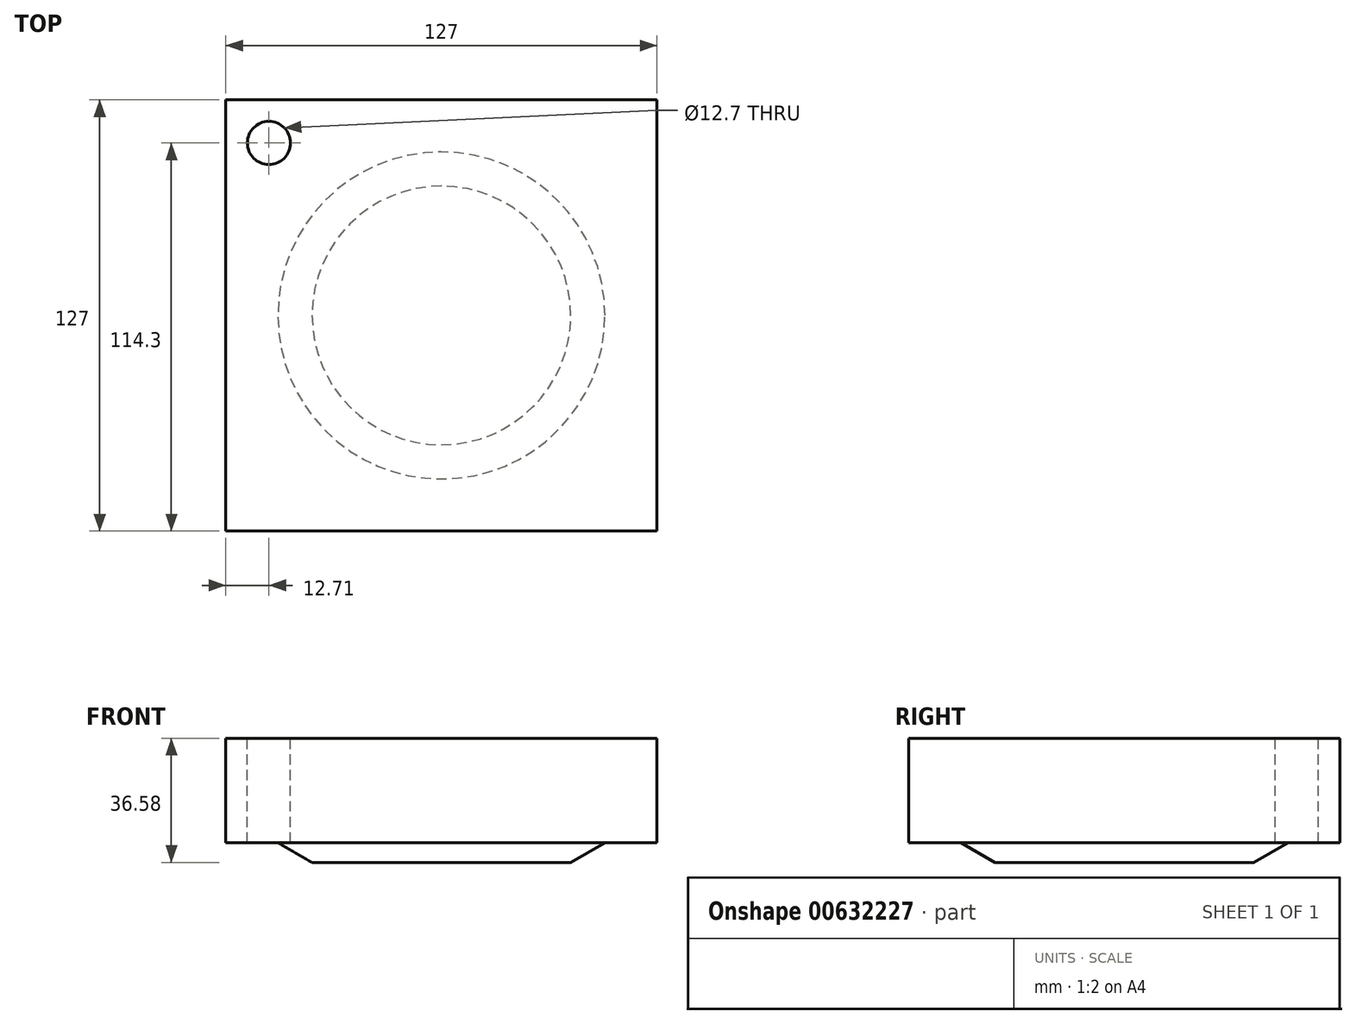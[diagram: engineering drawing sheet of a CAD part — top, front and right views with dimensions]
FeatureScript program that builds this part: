
annotation { "Feature Type Name" : "Feature", "Feature Type Description" : "" }
export const myFeature = defineFeature(function(context is Context, id is Id, definition is map)
    precondition{}
    {
        {
            var Q0;
            Q0=qCreatedBy(makeId("Front.planeOp"),FACE);
            var sketch = newSketch(context, id + "F0", { "sketchPlane" : qUnion([Q0])});
            skLineSegment(sketch, "E0", {"start": v(38.1, 1.52) * mm, "end": v(0, 1.52) * mm});
            skLineSegment(sketch, "E1", {"start": v(0, 1.52) * mm, "end": v(0, 0) * mm});
            skLineSegment(sketch, "E2", {"start": v(38.1, 1.52) * mm, "end": v(48.16, 7.33) * mm});
            skPoint(sketch, "E3.middle", {"position": v(0, 1.52) * mm});
            skLineSegment(sketch, "E4", {"start": v(0, 1.52) * mm, "end": v(38.1, 1.52) * mm});
            skLineSegment(sketch, "E5", {"start": v(48.16, 7.33) * mm, "end": v(92.57, 7.33) * mm});
            skLineSegment(sketch, "E6", {"start": v(92.57, 7.33) * mm, "end": v(92.57, 0) * mm});
            skLineSegment(sketch, "E7", {"start": v(0, 0) * mm, "end": v(92.57, 0) * mm});
            skSolve(sketch);
        }
        {
            var Q0;
            Q0=qCreatedBy(makeId("Front.planeOp"),FACE);
            var sketch = newSketch(context, id + "F1", { "sketchPlane" : qUnion([Q0])});
            skLineSegment(sketch, "E8.bottom", {"start": v(-63.5, 0) * mm, "end": v(63.5, 0) * mm});
            skLineSegment(sketch, "E8.top", {"start": v(-63.5, 38.1) * mm, "end": v(63.5, 38.1) * mm});
            skLineSegment(sketch, "E8.left", {"start": v(-63.5, 0) * mm, "end": v(-63.5, 38.1) * mm});
            skLineSegment(sketch, "E8.right", {"start": v(63.5, 0) * mm, "end": v(63.5, 38.1) * mm});
            skSolve(sketch);
        }
        {
            var Q0;
            Q0=makeQuery(id+"F1.imprint","IMPRINT",FACE,{"disambiguationData":[TD([[makeQuery(id+"F1.imprint","IMPRINT",EDGE,{"derivedFrom":sQuery(id+"F1.wireOp",EDGE,"E8.bottom")}),1.0]])]});
            extrude(context, id + "F2", {"entities" : qUnion([Q0]), "endBound" : BoundingType.SYMMETRIC, "depth" : 127 * mm, "offsetDistance" : 25.4 * mm});
        }
        {
            var Q0;
            Q0=makeQuery(id+"F0.imprint","IMPRINT",FACE,{"disambiguationData":[TD([[makeQuery(id+"F0.imprint","IMPRINT",EDGE,{"derivedFrom":sQuery(id+"F0.wireOp",EDGE,"E1")}),1.0]])]});
            var Q1;
            Q1=sQuery(id+"F0.wireOp",EDGE,"E1");
            revolve(context, id + "F3", {"operationType" : NewBodyOperationType.REMOVE, "entities" : qUnion([Q0]), "axis" : qUnion([Q1]), "revolveType" : RevolveType.FULL, "oppositeDirection" : true});
        }
        {
            var Q0;
            Q0=qCreatedBy(makeId("Top.planeOp"),FACE);
            var sketch = newSketch(context, id + "F4", { "sketchPlane" : qUnion([Q0])});
            skLineSegment(sketch, "E9", {"start": v(-50.8, 50.8) * mm, "end": v(0, 50.8) * mm});
            skLineSegment(sketch, "E10", {"start": v(-50.8, 50.8) * mm, "end": v(-50.8, 0) * mm});
            skCircle(sketch, "E11", {"center": v(-50.8, 50.8) * mm, "radius": 6.35 * mm});
            skSolve(sketch);
        }
        {
            var Q0;
            Q0=qSketchRegion(id+"F4",true);
            extrude(context, id + "F5", {"entities" : qUnion([Q0]), "operationType" : NewBodyOperationType.REMOVE, "endBound" : BoundingType.SYMMETRIC, "oppositeDirection" : true, "depth" : 101.6 * mm, "offsetDistance" : 25.4 * mm});
        }
    });
